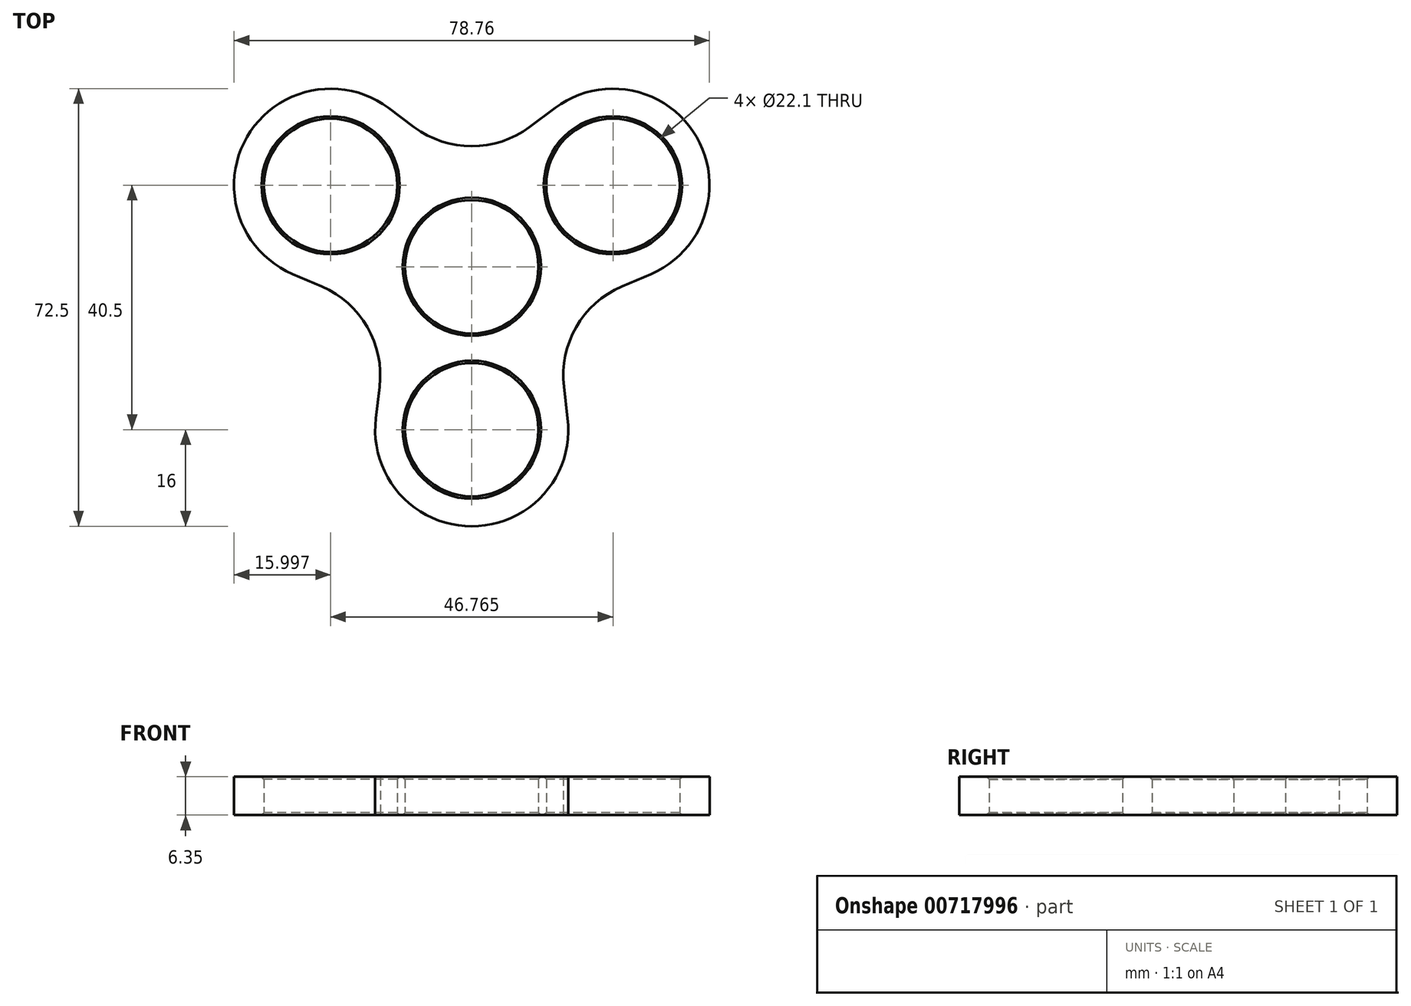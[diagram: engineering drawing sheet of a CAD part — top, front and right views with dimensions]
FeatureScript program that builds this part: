
annotation { "Feature Type Name" : "Feature", "Feature Type Description" : "" }
export const myFeature = defineFeature(function(context is Context, id is Id, definition is map)
    precondition{}
    {
        {
            var Q0;
            Q0=qCreatedBy(makeId("Top.planeOp"),FACE);
            var sketch = newSketch(context, id + "F0", { "sketchPlane" : qUnion([Q0])});
            skLineSegment(sketch, "E0", {"start": v(0, 0) * mm, "end": v(0, -27) * mm, "construction": true});
            skLineSegment(sketch, "E1", {"start": v(0, 0) * mm, "end": v(23.38, 13.5) * mm, "construction": true});
            skLineSegment(sketch, "E2", {"start": v(0, 0) * mm, "end": v(-23.38, 13.5) * mm, "construction": true});
            skCircle(sketch, "E3", {"center": v(-23.38, 13.5) * mm, "radius": 11.05 * mm});
            skCircle(sketch, "E4", {"center": v(23.38, 13.5) * mm, "radius": 11.05 * mm});
            skCircle(sketch, "E5", {"center": v(0, -27) * mm, "radius": 11.05 * mm});
            skCircle(sketch, "E6", {"center": v(0, 0) * mm, "radius": 11.05 * mm});
            skArc(sketch, "E7", {"start": v(-13.8, 26.32) * mm, "mid": v(-37.24, 21.5) * mm, "end": v(-29.7, -1.2) * mm});
            skLineSegment(sketch, "E8", {"start": v(-9.58, 23.16) * mm, "end": v(-13.8, 26.32) * mm});
            skLineSegment(sketch, "E9", {"start": v(9.58, 23.16) * mm, "end": v(13.8, 26.32) * mm});
            skPoint(sketch, "E10.visualSharp", {"position": v(0, 16) * mm});
            skArc(sketch, "E10.filletArc", {"start": v(-9.58, 23.16) * mm, "mid": v(0, 19.97) * mm, "end": v(9.58, 23.16) * mm});
            skLineSegment(sketch, "E11", {"start": v(0, 0) * mm, "end": v(-43.3, -25) * mm, "construction": true});
            skLineSegment(sketch, "E12", {"start": v(0, 0) * mm, "end": v(43.3, -25) * mm, "construction": true});
            skLineSegment(sketch, "E13", {"start": v(15.27, -19.87) * mm, "end": v(15.89, -25.11) * mm});
            skLineSegment(sketch, "E14", {"start": v(-15.27, -19.87) * mm, "end": v(-15.89, -25.11) * mm});
            skLineSegment(sketch, "E15", {"start": v(-24.84, -3.28) * mm, "end": v(-29.7, -1.2) * mm});
            skLineSegment(sketch, "E16", {"start": v(24.84, -3.28) * mm, "end": v(29.7, -1.2) * mm});
            skPoint(sketch, "E17.visualSharp", {"position": v(13.86, -8) * mm});
            skArc(sketch, "E17.filletArc", {"start": v(24.84, -3.28) * mm, "mid": v(17.3, -9.99) * mm, "end": v(15.27, -19.87) * mm});
            skPoint(sketch, "E18.visualSharp", {"position": v(-13.86, -8) * mm});
            skArc(sketch, "E18.filletArc", {"start": v(-15.27, -19.87) * mm, "mid": v(-17.3, -9.99) * mm, "end": v(-24.84, -3.28) * mm});
            skArc(sketch, "E19.trimOffspring", {"start": v(29.7, -1.2) * mm, "mid": v(37.24, 21.5) * mm, "end": v(13.8, 26.32) * mm});
            skArc(sketch, "E20.trimOffspring", {"start": v(-15.89, -25.11) * mm, "mid": v(0, -43) * mm, "end": v(15.89, -25.11) * mm});
            skCircle(sketch, "E21", {"center": v(-23.38, 13.5) * mm, "radius": 11 * mm});
            skCircle(sketch, "E22", {"center": v(23.38, 13.5) * mm, "radius": 11 * mm});
            skSolve(sketch);
        }
        {
            var Q0;
            Q0=qSketchRegion(id+"F0",true);
            extrude(context, id + "F1", {"entities" : qUnion([Q0]), "depth" : 6.35 * mm, "offsetDistance" : 25 * mm});
        }
        {
            var Q0;
            Q0=makeQuery(id+"F1.opExtrude","CAP_EDGE",EDGE,{"disambiguationData":[OSD([sQuery(id+"F0.wireOp",EDGE,"E6")])],"isStart":false});
            var Q1;
            Q1=makeQuery(id+"F1.opExtrude","CAP_EDGE",EDGE,{"disambiguationData":[OSD([sQuery(id+"F0.wireOp",EDGE,"E6")])],"isStart":true});
            var Q2;
            Q2=makeQuery(id+"F1.opExtrude","CAP_EDGE",EDGE,{"disambiguationData":[OSD([sQuery(id+"F0.wireOp",EDGE,"E5")])],"isStart":false});
            var Q3;
            Q3=makeQuery(id+"F1.opExtrude","CAP_EDGE",EDGE,{"disambiguationData":[OSD([sQuery(id+"F0.wireOp",EDGE,"E5")])],"isStart":true});
            var Q4;
            Q4=makeQuery(id+"F1.opExtrude","CAP_EDGE",EDGE,{"disambiguationData":[OSD([sQuery(id+"F0.wireOp",EDGE,"E3")])],"isStart":false});
            var Q5;
            Q5=makeQuery(id+"F1.opExtrude","CAP_EDGE",EDGE,{"disambiguationData":[OSD([sQuery(id+"F0.wireOp",EDGE,"E3")])],"isStart":true});
            var Q6;
            Q6=makeQuery(id+"F1.opExtrude","CAP_EDGE",EDGE,{"disambiguationData":[OSD([sQuery(id+"F0.wireOp",EDGE,"E4")])],"isStart":false});
            var Q7;
            Q7=makeQuery(id+"F1.opExtrude","CAP_EDGE",EDGE,{"disambiguationData":[OSD([sQuery(id+"F0.wireOp",EDGE,"E4")])],"isStart":true});
            chamfer(context, id + "F2", {"entities" : qUnion([Q0, Q1, Q2, Q3, Q4, Q5, Q6, Q7]), "width" : 0.4 * mm, "tangentPropagation" : true});
        }
    });
